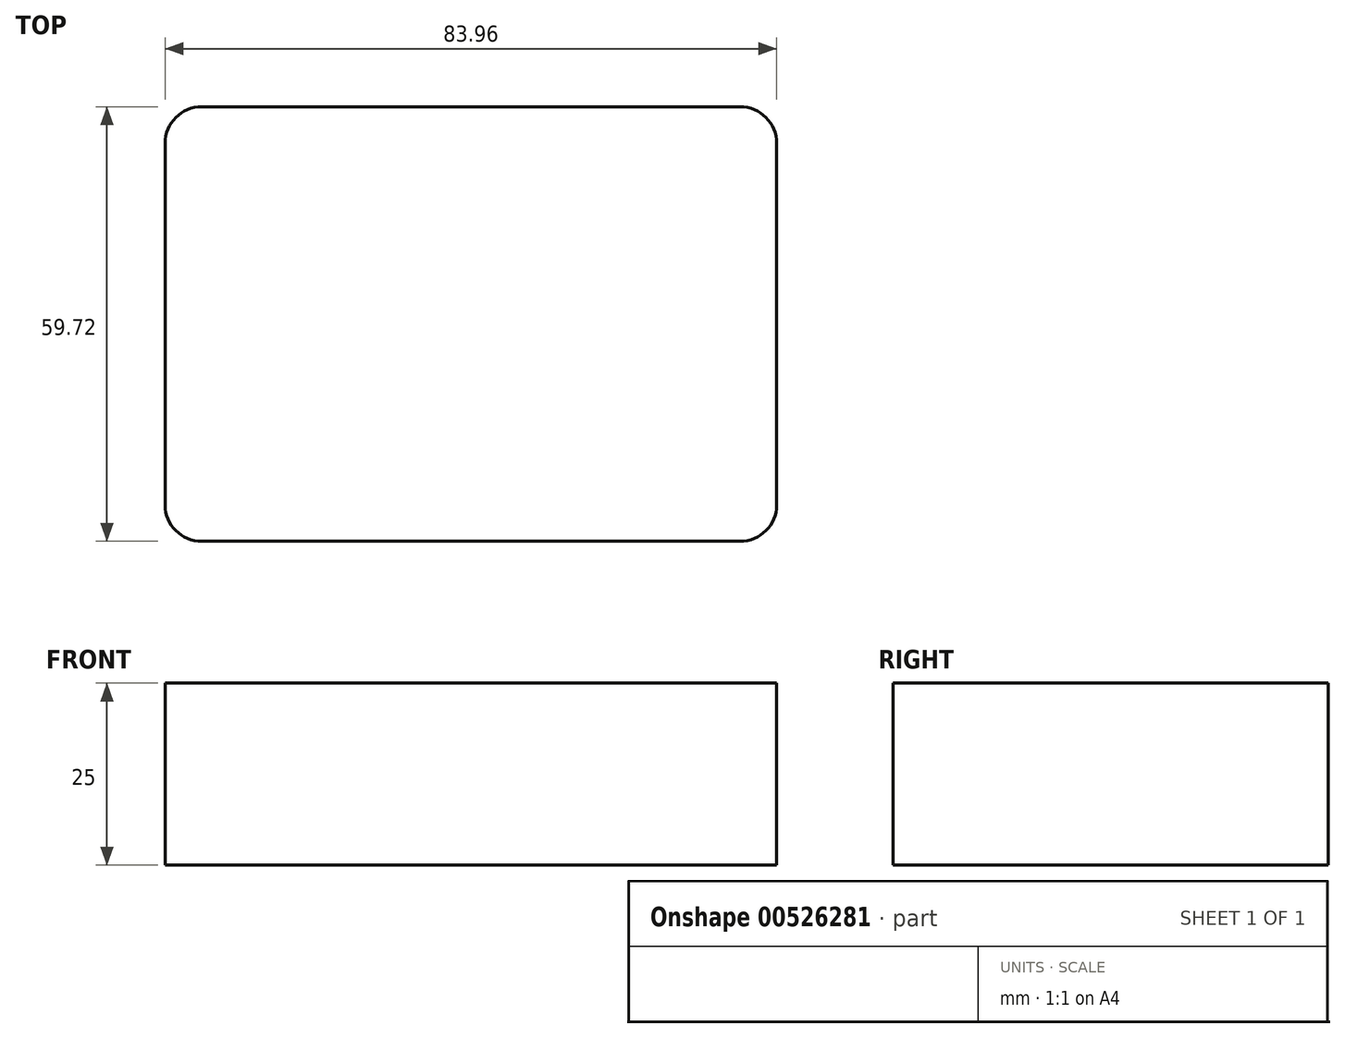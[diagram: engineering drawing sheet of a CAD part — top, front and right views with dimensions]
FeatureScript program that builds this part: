
annotation { "Feature Type Name" : "Feature", "Feature Type Description" : "" }
export const myFeature = defineFeature(function(context is Context, id is Id, definition is map)
    precondition{}
    {
        {
            var Q0;
            Q0=qCreatedBy(makeId("Top.planeOp"),FACE);
            var sketch = newSketch(context, id + "F0", { "sketchPlane" : qUnion([Q0])});
            skLineSegment(sketch, "E0.bottom", {"start": v(41.98, -29.86) * mm, "end": v(-41.98, -29.86) * mm});
            skLineSegment(sketch, "E0.top", {"start": v(41.98, 29.86) * mm, "end": v(-41.98, 29.86) * mm});
            skLineSegment(sketch, "E0.left", {"start": v(41.98, -29.86) * mm, "end": v(41.98, 29.86) * mm});
            skLineSegment(sketch, "E0.right", {"start": v(-41.98, -29.86) * mm, "end": v(-41.98, 29.86) * mm});
            skPoint(sketch, "E0.middle", {"position": v(0, 0) * mm});
            skSolve(sketch);
        }
        {
            var Q0;
            Q0=makeQuery(id+"F0.imprint","IMPRINT",FACE,{"disambiguationData":[TD([[makeQuery(id+"F0.imprint","IMPRINT",EDGE,{"derivedFrom":sQuery(id+"F0.wireOp",EDGE,"E0.bottom")}),-1.0]])]});
            extrude(context, id + "F1", {"entities" : qUnion([Q0]), "depth" : 25 * mm, "offsetDistance" : 25 * mm});
        }
        {
            var Q0;
            Q0=makeQuery(id+"F1.opExtrude","SWEPT_EDGE",EDGE,{"disambiguationData":[OSD([sQuery(id+"F0.wireOp",EDGE,"E0.bottom"),sQuery(id+"F0.wireOp",EDGE,"E0.right")])]});
            var Q1;
            Q1=makeQuery(id+"F1.opExtrude","SWEPT_EDGE",EDGE,{"disambiguationData":[OSD([sQuery(id+"F0.wireOp",EDGE,"E0.bottom"),sQuery(id+"F0.wireOp",EDGE,"E0.left")])]});
            var Q2;
            Q2=makeQuery(id+"F1.opExtrude","SWEPT_EDGE",EDGE,{"disambiguationData":[OSD([sQuery(id+"F0.wireOp",EDGE,"E0.top"),sQuery(id+"F0.wireOp",EDGE,"E0.left")])]});
            var Q3;
            Q3=makeQuery(id+"F1.opExtrude","SWEPT_EDGE",EDGE,{"disambiguationData":[OSD([sQuery(id+"F0.wireOp",EDGE,"E0.top"),sQuery(id+"F0.wireOp",EDGE,"E0.right")])]});
            fillet(context, id + "F2", {"entities" : qUnion([Q0, Q1, Q2, Q3]), "radius" : 5 * mm, "tangentPropagation" : true, "allowEdgeOverflow" : false});
        }
    });
